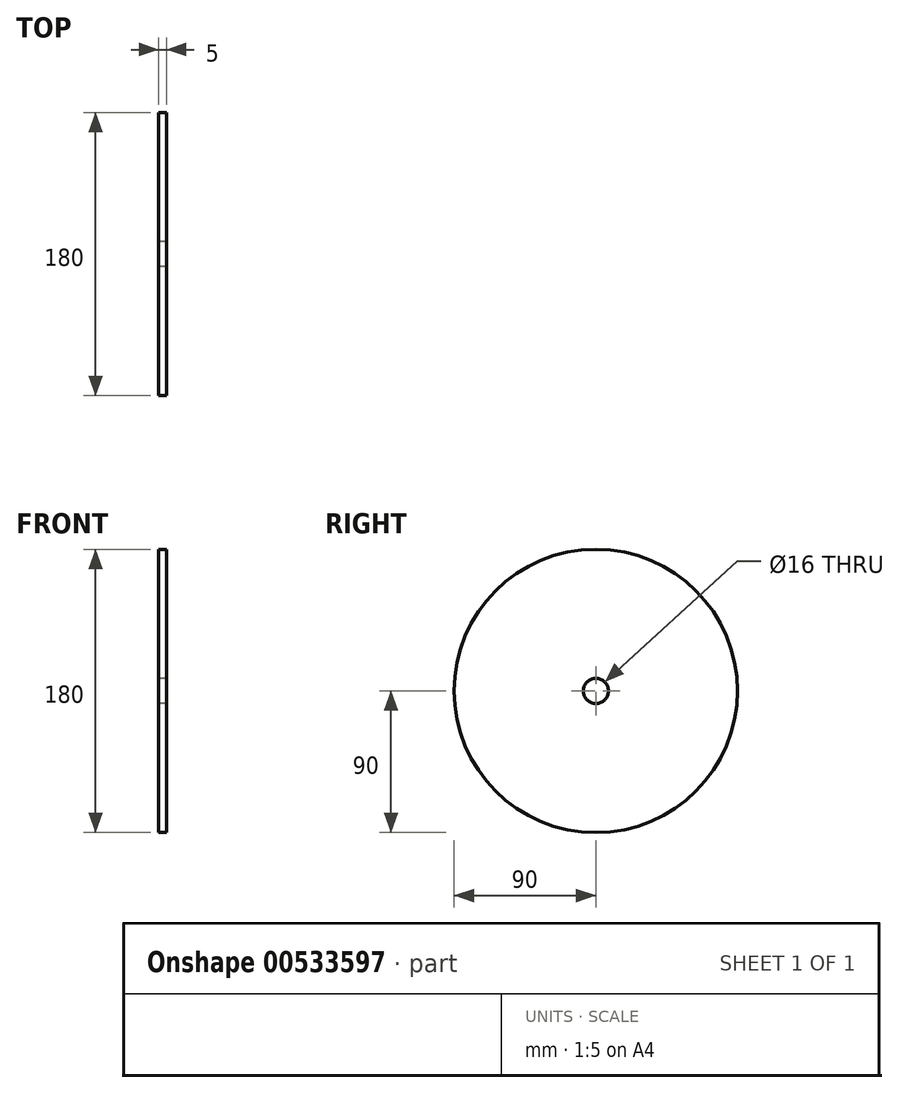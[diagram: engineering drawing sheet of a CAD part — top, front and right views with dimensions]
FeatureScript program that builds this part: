
annotation { "Feature Type Name" : "Feature", "Feature Type Description" : "" }
export const myFeature = defineFeature(function(context is Context, id is Id, definition is map)
    precondition{}
    {
        {
            var Q0;
            Q0=qCreatedBy(makeId("Right.planeOp"),FACE);
            var sketch = newSketch(context, id + "F0", { "sketchPlane" : qUnion([Q0])});
            skCircle(sketch, "E0", {"center": v(0, 0) * mm, "radius": 90 * mm});
            skCircle(sketch, "E1", {"center": v(0, 0) * mm, "radius": 8 * mm});
            skSolve(sketch);
        }
        {
            var Q0;
            Q0=qSketchRegion(id+"F0",true);
            extrude(context, id + "F1", {"entities" : qUnion([Q0]), "depth" : 5 * mm});
        }
    });
